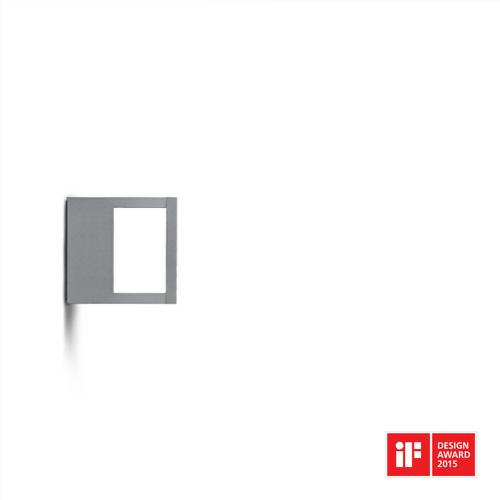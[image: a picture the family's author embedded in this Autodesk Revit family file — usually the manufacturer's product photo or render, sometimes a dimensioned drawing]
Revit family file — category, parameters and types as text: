
# Revit family: SIMES_S.7282W_Cool Square applique
name_source: partatom
category: Lighting Fixtures
revit_build: Autodesk Revit 2016 (Build: 20150714_1515(x64)
units: mm (PartAtom-declared; Revit-internal decimal feet)

## family parameters
Cut with Voids When Loaded = No
Host = Face
Light Source = Yes
OmniClass Number = 23.80.70.14
OmniClass Title = Luminaries for External Lighting
Part Type = Normal
Room Calculation Point = No
Round Connector Dimension = Use Diameter
Shared = No

## types (1)
- SIMES_S.7282W_Cool Square applique
    Approval mark = CE, ENEC
    Assembly Code = D5020
    Color Filter = 16777215
    Color Rendering Index = CRI 90
    Colour Temperature = 3000
    Control Gear = electronic transformer
    Default Elevation = 1219 mm
    Description = MICROCOOL SQUARE APPLIQUE
Art. S.7282W
MODULES LED 3000K  230V CRI 90 MacAdam step 3
Rated luminaire luminous flux: 204lm
Rated input power: 7W
Luminaire efficacy: 29lm/W
Electronic ballast 220÷240V 0/50/60Hz
CE - ENEC 03

PRODUCT TYPE
Wall mounted luminaire or Bollard fitting ( bollard version ). IP rating IP 54
MATERIAL CHARACTERISTICS
Aluminium die cast housing in EN AB-47100 (low copper content) with high resistance against corrosion. Extruded EN AW-6060 aluminium structure (bollard version) with high corrosion resistance. Stone wash surface treatment prior to painting process. A4 grade Stainless Steel screws with 2,5-3% molybdenum content which increases the resistance against corrosion. Silicone gaskets. Painting Process : 3 Step Process
1) Surface treatment with BONDERITE. A heavy metal free chemical surface treatment containing ceramic nano particles giving a cohesive, inorganic and highly dense protective coating. 2) PRE POLYMERIZATION a process of introducing an epoxy primer with excellent characteristics to the paint which also offers very high resistance to oxidation due to its Zinc content. 3) POLYMERIZATION a process with the application of polyester powder with high resistance against UV rays and harsh weather conditions. Resistance test protection for Marine applications for 1200h.  Mechanical resistance IK 06
LIGHTING PERFORMANCE
Toughened glass diffuser. LOR --. Colour rendering index  CRI 90, Colour stability step  MacAdam step 3. 
WIRING
MICROCOOL hard wired with H07RN-F cable . MINICOOL and COOL is supplied with single cable entry.  Isolation: CLASS I . Available colours: White (cod.01), Aluminium grey (cod.14). Weight: 0.89 Kg Glow Wire test: --
Lamp included.
LOOK and COOL REGISTERED DESIGN
This luminaire contains built-in LED modules with energy class: A, A+, A++. In case of damage or malfunction please contact the manufacturer to receive additional instructions on how to replace and relative spare parts to order. The LED modules cannot be handled in the luminaire by the end user (Regulation UE 874/2012).
LED circuit boards are engineered accordingly to actual Lumen Maintenance regulation (LM80) and Technical Memorandum (TM21) where uniformity and quality of light is 50.000 hours referred to L70  B20 Ta 25°C.Lifecycle refers to LED circuit boards only, all others components of the luminaire are excluded.

EMERGENCY VERSIONS The fittings operates both on AC ( 50/60Hz ) and DC ( 0Hz ) voltage.
    Dimming Lamp Color Temperature Shift = <None>
    Frequency = 0/50/60Hz
    IFC Classification = Light Fixture
    IK Rating = IK 06
    Lamp = LED
    Lamp Light Flux = 545
    Lamp count = 1
    Last Update = 02/08/2018 10:14:01
    Lifetime = 50000 L70 B20 Ta 25°C
    Light Output Ratio = 100
    Luminous efficacy = 29,1
    Manufacturer = SIMES
    Masterformat 2014 Code = 26 56 00
    Masterformat 2014 Description = Exterior Lighting
    Model = S.7282W
    Mounting Place = Wall
    Mounting Type = Surface mounted
    NBS Reference Code = 49
    NBS Reference Description = Luminaries And Lamps
    OmniClass Code = 23-35 47 11
    OmniClass Description = Lighting Fixture
    Photometric Web File = S7282W.ies
    Product Group = wall-mounted luminaire
    Product Name = Cool Square applique
    Protection Class = Protection class I
    Protection Degree = IP 54
    System Light Flux = 204
    System Power = 7
    Tilt Angle = 90.00°
    Type Comments = SIMES S.p.A. - All rights reserved
    Type Image = microcool_applique_quadrato.jpg
    UNSPSC Code = 3911
    URL = http://www.simes.it
    Uniclass 1.4 Code = YJ73
    Uniclass 1.4 Description = Luminaries and lamps
    Uniclass 2.0 Code = PR-49
    Uniclass 2.0 Description = Luminaries and lamps
    Uniclass 2015 Code = EF_70_80
    Uniclass 2015 Name = Lighting
    Uniformat II Code = D5020
    Uniformat II Description = Lighting & Branch Wiring
    Voltage = 220÷240V

## geometry (parser evidence)
native form markers: Sweep x1
no freeform markers — native parametric forms only
